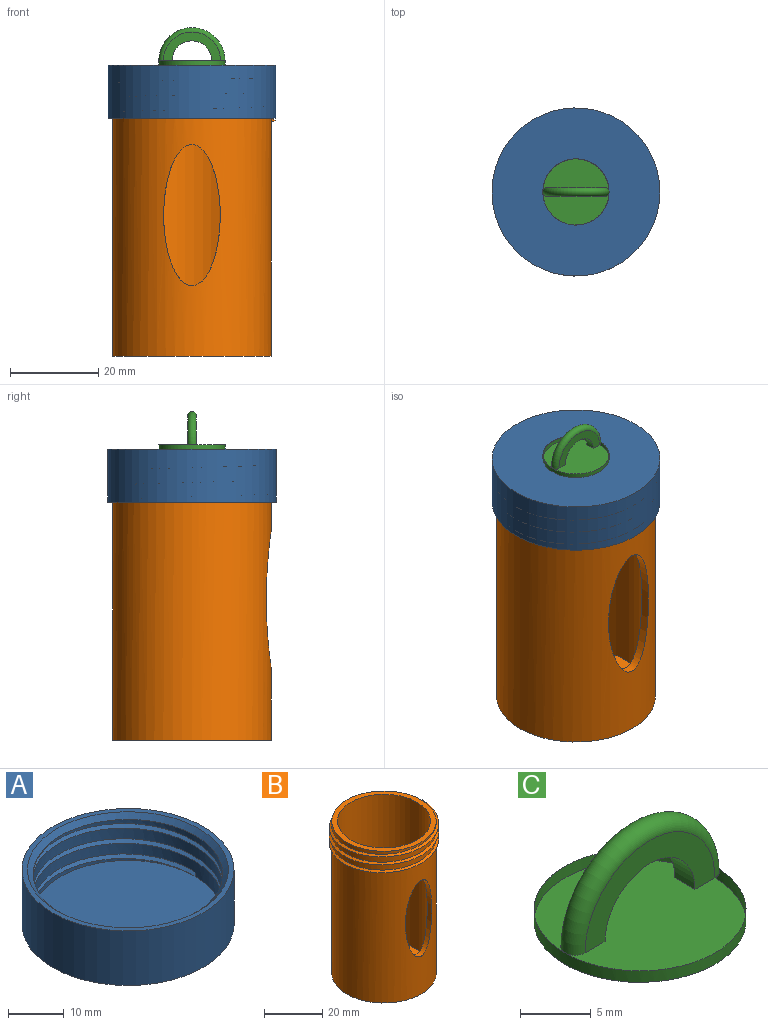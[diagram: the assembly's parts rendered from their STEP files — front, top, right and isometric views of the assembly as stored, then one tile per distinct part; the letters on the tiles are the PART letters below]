
ASSEMBLY  parts=3 mates=2
PART A: 10 faces, bbox 38.1x41.4x12.4 mm
  f0: cylinder r=17.05mm len=34.1mm, axis (0,0,-1), area 691mm2, adj f4,f5,f6,f7,f8,f9
  f1: plane 38.1x38.1mm, normal (0,0,-1), area 1140.1mm2, adj f2
  f2: cylinder r=19.05mm len=38.1mm, axis (0,0,-1), area 1436.3mm2, adj f1,f3
  f3: plane 38.1x38.1mm, normal (0,0,1), area 116.6mm2, adj f2,f9
  f4: plane 34.1x34.1mm, normal (0,0,1), area 913.3mm2, adj f0
  f5: bspline ~41.38x35.83mm, area 302.8mm2, adj f0,f6,f7,f8
  f6: bspline ~41.38x35.83mm, area 286.2mm2, adj f0,f5,f7,f9
  f7: plane 1x0.87mm, normal (0,1,0), area 0.4mm2, adj f0,f5,f6
  f8: cone r=18.05mm half-angle=45deg, axis (0,0,1), area 7.1mm2, adj f0,f5,f9
  f9: cone r=18.05mm half-angle=45deg, axis (0,0,1), area 128.8mm2, adj f0,f3,f6,f8
PART B: 13 faces, bbox 37.7x43.6x64 mm
  f0: cylinder r=18mm len=58mm, axis (0,0,-1), area 5986.2mm2, adj f1,f5,f8,f10,f11,f12
  f1: cylinder r=18mm len=36mm, axis (0,0,-1), area 263.9mm2, adj f0,f2,f11,f12
  f2: cylinder r=18mm len=36mm, axis (0,0,-1), area 273.3mm2, adj f1,f3,f6,f9,f11,f12
  f3: cylinder r=18mm len=36mm, axis (0,0,-1), area 47.1mm2, adj f2,f6,f11
  f4: cylinder r=16mm len=62mm, axis (0,0,-1), area 5903.1mm2, adj f6,f7,f8
  f5: plane 36x36mm, normal (0,0,-1), area 1017.9mm2, adj f0
  f6: plane 36x36mm, normal (0,0,1), area 213.6mm2, adj f2,f3,f4
  f7: plane 32x32mm, normal (0,0,1), area 804.2mm2, adj f4
  f8: extruded ~32.01x12.84mm, area 154.4mm2, adj f0,f4
  f9: plane 1x0.87mm, normal (0,1,0), area 0.4mm2, adj f2,f11,f12
  f10: plane 1x0.87mm, normal (0,-1,0), area 0.4mm2, adj f0,f11,f12
  f11: bspline ~43.57x37.73mm, area 347.6mm2, adj f0,f1,f2,f3,f9,f10,f12
  f12: bspline ~43.57x37.73mm, area 347.6mm2, adj f0,f1,f2,f9,f10,f11
PART C: 7 faces, bbox 16.2x15x9.1 mm
  f0: cylinder r=7.5mm len=15mm, axis (0,0,-1), area 47.1mm2, adj f1,f2
  f1: plane 15x15mm, normal (0,0,1), area 165.6mm2, adj f0,f3,f4,f5,f6
  f2: plane 15x15mm, normal (0,0,-1), area 176.7mm2, adj f0
  f3: cylinder r=4.5mm len=9mm, axis (0,1,0), area 28.3mm2, adj f1,f4,f5
  f4: plane 13x6.5mm, normal (0,-1,0), area 34.6mm2, adj f1,f3,f6
  f5: plane 13x6.5mm, normal (0,1,0), area 34.6mm2, adj f1,f3,f6
  f6: torus R=6.5mm, axis (0,-1,0), area 70.4mm2, adj f1,f4,f5
PLACE A rot(axis=(0,-1,0),180deg) t=(-30.5,-20.46,106.58)mm
PLACE B t=(19.5,-20.46,44.58)mm
PLACE C t=(19.5,-20.46,108.58)mm
MATE fastened C.f0 <-> A.f0  axis (0,0,-1) through (19.5,-20.46,108.58)mm
MATE revolute A.f0 <-> B.f0  axis (0,0,-1) through (19.5,-20.46,106.58)mm
